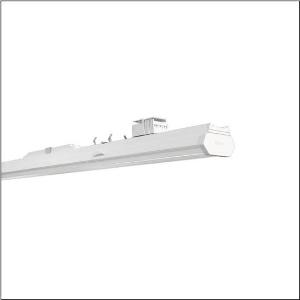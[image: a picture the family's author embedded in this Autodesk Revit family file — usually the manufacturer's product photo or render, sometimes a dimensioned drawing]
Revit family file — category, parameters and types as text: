
# Revit family: licross_r__11_protected_mo_51tp12cn49xg_4f1c
name_source: partatom
category: Lighting Fixtures
units: mm (PartAtom-declared; Revit-internal decimal feet)

## family parameters
Cut with Voids When Loaded = No
Host = Face
Light Source = No
Part Type = Normal
Room Calculation Point = No
Round Connector Dimension = Use Diameter
Shared = No

## types (1)
- --- (1 x LED, 9070 lm, 49.4 W, 4000K)
    Apparent Load = 49 VA
    CIE Flux Codes = 73 92 98 99 100
    Color Rendering = 80
    Color Temperature = 4000K
    Default Elevation = 1800 mm
    Description = Licross® 11 Protected MO, luminaire insert, of sheet steel, galvanised, coil coated, white, length: 1.500mm, width: 90mm, height: 101mm, LED rated luminous flux: 9.070lm, light colour: 840, control gear: ON/OFF Multilumen, CLOi, with plug, 3-pole, with phase selection, mains connection: 220..240V, AC, 50/60Hz, start of lifetime: 49W, end of service life: 55W, halogen-free wiring, primary light control with lens, of plastic, primary optical cover: cover, of PMMA, light emission: direct distribution, primary light characteristic: symmetric, protection rating (complete): IP64, insulation class (complete): insulation class I (protective earthing), certification: CE, ENEC, VDE, UKCA, protection symbol: D if used in an environment with conductive dust loads with corresponding accessories, impact resistance: IK06, permissible ambient temperature for indoor applications: -35..+40°C, corresponds to IFS (International Featured Standards) requirements for safety and quality in the food industry, reducing of maximum allowable ambient temperature of 5°C with ceiling mounting, LABS conformity tested according to VDMA 24364:2018-05, packaging unit: 1 piece
    Height = 92 mm
    Lamp = 1 x LED
    Lamp Light Flux = 9070 lm
    Lamp Power = 49.4 W
    Lamp count = 1
    Length = 1500 mm
    Luminous efficacy = 184 lm/W
    Manufacturer = Siteco
    ModVariant = No
    Model = 51TP12CN49XG
    Mounting Place = Ceiling
    Mounting Type = Pendant
    Number of Poles = 1
    OnlyDefault = Yes
    Power Factor = 1
    Product Name = Licross® 11 Protected MO
    Product group = luminaire insert
    ProductGroupID = 901
    Protection Class = Protection class I
    Protection Degree = IP 64
    RLX_Detail_Level = 1
    RLX_Emergency_Light_Flux = 0 lm
    RLX_Emergency_Type = 0
    RLX_Emergency_Type_DB = No
    RlxData = <blob elided: 22061 chars, md5=cfec7d3d>
    Socket = socket
    Standby Power = 0 W
    System Light Flux = 9070 lm
    System Power = 49 W
    Type Comments = factory setting: luminous flux: 100 % | (A | C | E) | 113 mA
    Type Image = l_1256148.jpg
    URL = http://relux.com
    VarID = @adj_019395
    Voltage = 0 V
    Weight = 0.00 kg
    Width = 88 mm

## geometry (parser evidence)
native form markers: Blend x4, Sweep x12
no freeform markers — native parametric forms only
